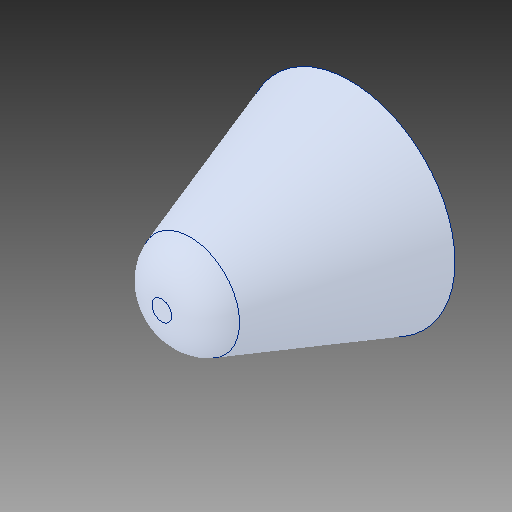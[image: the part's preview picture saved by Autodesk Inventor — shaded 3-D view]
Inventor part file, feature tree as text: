
AUTODESK INVENTOR PART (.ipt)
format: ipt  version: 2019 (Build 230136000, 136)  size: 110,080 bytes
history: mixed  units: mm
features: other x1, fillet x1, imported_body x1
ambient origin geometry x8: Origin, YZ Plane, XZ Plane, XY Plane, X Axis, Y Axis, Z Axis, Center Point
bodies: Body1 (imported_parasolid)
feature tree (3):
  other  "Твердое тело1"
  fillet  "Fillet1"  [1 undecoded]
  imported_body  NMx_Import_Brep_tag  [imported B-rep: ~4 faces, bbox_mm=[0.73655, 0.0, 0.9]]
note: 1 required parameter value undecoded (feature->parameter linkage not recoverable at this tier; creation-order binding heuristic only, values carry confidence <= 0.55)
